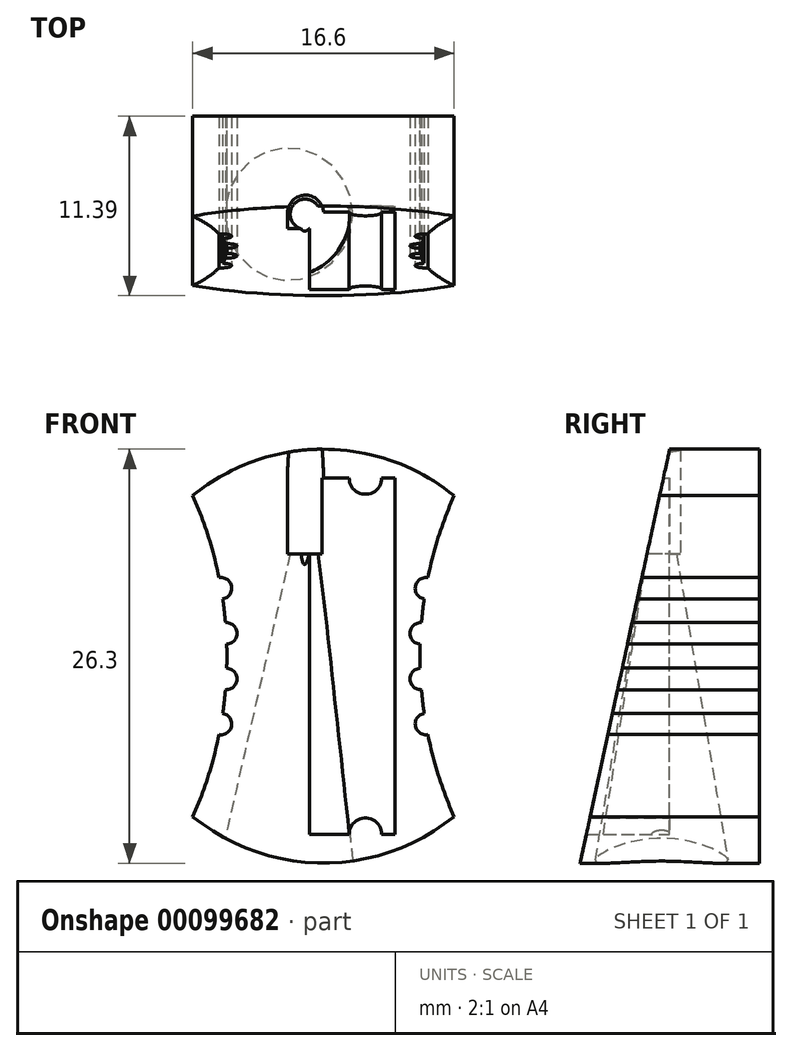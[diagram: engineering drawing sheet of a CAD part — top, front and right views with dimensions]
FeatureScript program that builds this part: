
annotation { "Feature Type Name" : "Feature", "Feature Type Description" : "" }
export const myFeature = defineFeature(function(context is Context, id is Id, definition is map)
    precondition{}
    {
        {
            var Q0;
            Q0=qCreatedBy(makeId("Front.planeOp"),FACE);
            var sketch = newSketch(context, id + "F0", { "sketchPlane" : qUnion([Q0])});
            skArc(sketch, "E0", {"start": v(-6.13, 0) * mm, "mid": v(-6.68, 5.21) * mm, "end": v(-8.3, 10.2) * mm});
            skPoint(sketch, "E0.first.point", {"position": v(-8.3, 10.2) * mm});
            skPoint(sketch, "E0.second.point", {"position": v(-6.13, 0) * mm});
            skPoint(sketch, "E0.third.point", {"position": v(-8.3, -10.2) * mm});
            skArc(sketch, "E1", {"start": v(0, 13.15) * mm, "mid": v(-4.4, 12.4) * mm, "end": v(-8.3, 10.2) * mm});
            skPoint(sketch, "E1.second.point", {"position": v(0, 13.15) * mm});
            skArc(sketch, "E2.MirrorCS", {"start": v(0, 13.15) * mm, "mid": v(4.4, 12.4) * mm, "end": v(8.3, 10.2) * mm});
            skArc(sketch, "E3.MirrorCS", {"start": v(6.13, 0) * mm, "mid": v(6.68, 5.21) * mm, "end": v(8.3, 10.2) * mm});
            skArc(sketch, "E4.MirrorCS", {"start": v(6.13, 0) * mm, "mid": v(6.68, -5.21) * mm, "end": v(8.3, -10.2) * mm});
            skArc(sketch, "E5.MirrorCS", {"start": v(0, -13.15) * mm, "mid": v(4.4, -12.4) * mm, "end": v(8.3, -10.2) * mm});
            skArc(sketch, "E6.MirrorCS", {"start": v(0, -13.15) * mm, "mid": v(-4.4, -12.4) * mm, "end": v(-8.3, -10.2) * mm});
            skArc(sketch, "E7.MirrorCS", {"start": v(-6.13, 0) * mm, "mid": v(-6.68, -5.21) * mm, "end": v(-8.3, -10.2) * mm});
            skSolve(sketch);
        }
        {
            var Q0;
            Q0 = qSketchRegion(id + "F0", true);
            extrude(context, id + "F1", {"entities" : qUnion([Q0]), "endBound" : BoundingType.SYMMETRIC, "depth" : 11.4 * mm});
        }
        {
            var Q0;
            Q0=qCreatedBy(makeId("Right.planeOp"),FACE);
            var sketch = newSketch(context, id + "F2", { "sketchPlane" : qUnion([Q0])});
            skLineSegment(sketch, "E8", {"start": v(0, 13.15) * mm, "end": v(-6, -14.56) * mm});
            skLineSegment(sketch, "E9", {"start": v(-6, -14.56) * mm, "end": v(-6, 13.15) * mm});
            skLineSegment(sketch, "E10", {"start": v(-6, 13.15) * mm, "end": v(0, 13.15) * mm});
            skSolve(sketch);
        }
        {
            var Q0;
            Q0=makeQuery(id+"F2.imprint","IMPRINT",FACE,{"disambiguationData":[TD([[makeQuery(id+"F2.imprint","IMPRINT",EDGE,{"derivedFrom":sQuery(id+"F2.wireOp",EDGE,"E8")}),-1.0]])]});
            var Q1;
            Q1=sQuery(id+"F2.wireOp",EDGE,"E10");
            extrude(context, id + "F3", {"entities" : qUnion([Q0]), "operationType" : NewBodyOperationType.REMOVE, "surfaceEntities" : qUnion([Q1]), "endBound" : BoundingType.SYMMETRIC, "oppositeDirection" : true, "depth" : 36.88 * mm});
        }
        {
            var Q0;
            Q0=qCreatedBy(makeId("Front.planeOp"),FACE);
            var sketch = newSketch(context, id + "F4", { "sketchPlane" : qUnion([Q0])});
            skCircle(sketch, "E11", {"center": v(-6.5, 4.3) * mm, "radius": 0.69 * mm});
            skCircle(sketch, "E12.MirrorC", {"center": v(-6.5, -4.3) * mm, "radius": 0.69 * mm});
            skCircle(sketch, "E13", {"center": v(-6.18, 1.45) * mm, "radius": 0.69 * mm});
            skCircle(sketch, "E14.MirrorC", {"center": v(-6.18, -1.45) * mm, "radius": 0.69 * mm});
            skCircle(sketch, "E15.MirrorC", {"center": v(6.5, 4.3) * mm, "radius": 0.69 * mm});
            skCircle(sketch, "E16.MirrorC", {"center": v(6.18, 1.45) * mm, "radius": 0.69 * mm});
            skCircle(sketch, "E17.MirrorC", {"center": v(6.18, -1.45) * mm, "radius": 0.69 * mm});
            skCircle(sketch, "E18.MirrorC", {"center": v(6.5, -4.3) * mm, "radius": 0.69 * mm});
            skSolve(sketch);
        }
        {
            var Q0;
            Q0 = qSketchRegion(id + "F4", true);
            extrude(context, id + "F5", {"entities" : qUnion([Q0]), "operationType" : NewBodyOperationType.REMOVE, "endBound" : BoundingType.SYMMETRIC, "oppositeDirection" : true, "depth" : 30.96 * mm});
        }
        {
            var Q0;
            Q0=qCreatedBy(makeId("Front.planeOp"),FACE);
            var sketch = newSketch(context, id + "F6", { "sketchPlane" : qUnion([Q0])});
            skLineSegment(sketch, "E19", {"start": v(4.56, 11.32) * mm, "end": v(4.56, 0) * mm});
            skLineSegment(sketch, "E20", {"start": v(-0.9, 0) * mm, "end": v(-0.9, 11.32) * mm});
            skLineSegment(sketch, "E21", {"start": v(-0.9, 11.32) * mm, "end": v(1.63, 11.32) * mm});
            skLineSegment(sketch, "E22.MirrorCS", {"start": v(4.56, -11.32) * mm, "end": v(4.56, 0) * mm});
            skLineSegment(sketch, "E23.MirrorCS", {"start": v(-0.9, -11.32) * mm, "end": v(1.63, -11.32) * mm});
            skLineSegment(sketch, "E24.MirrorCS", {"start": v(-0.9, 0) * mm, "end": v(-0.9, -11.32) * mm});
            skArc(sketch, "E25", {"start": v(1.63, 11.32) * mm, "mid": v(2.66, 10.28) * mm, "end": v(3.7, 11.32) * mm});
            skArc(sketch, "E26.MirrorC", {"start": v(1.63, -11.32) * mm, "mid": v(2.66, -10.28) * mm, "end": v(3.7, -11.32) * mm});
            skLineSegment(sketch, "E27.trimOffspring", {"start": v(3.7, -11.32) * mm, "end": v(4.56, -11.32) * mm});
            skLineSegment(sketch, "E28.trimOffspring", {"start": v(3.7, 11.32) * mm, "end": v(4.56, 11.32) * mm});
            skSolve(sketch);
        }
        {
            var Q0;
            Q0 = qSketchRegion(id + "F6", true);
            extrude(context, id + "F7", {"entities" : qUnion([Q0]), "operationType" : NewBodyOperationType.REMOVE, "depth" : 25 * mm});
        }
        {
            var Q0;
            Q0=qCreatedBy(makeId("Top.planeOp"),FACE);
            cPlane(context, id + "F8", {"entities" : qUnion([Q0]), "cplaneType" : CPlaneType.OFFSET, "offset" : 6.5 * mm, "width" : 150 * mm, "height" : 150 * mm});
        }
        {
            var Q0;
            Q0=qCreatedBy(id+"F8.planeOp",FACE);
            cPlane(context, id + "F9", {"entities" : qUnion([Q0]), "cplaneType" : CPlaneType.OFFSET, "offset" : 20 * mm, "oppositeDirection" : true, "width" : 150 * mm, "height" : 150 * mm});
        }
        {
            var Q0;
            Q0=qCreatedBy(id+"F9.planeOp",FACE);
            var sketch = newSketch(context, id + "F10", { "sketchPlane" : qUnion([Q0])});
            skCircle(sketch, "E29", {"center": v(-2.39, -0.52) * mm, "radius": 4.3 * mm});
            skSolve(sketch);
        }
        {
            var Q0;
            Q0=qCreatedBy(id+"F8.planeOp",FACE);
            var sketch = newSketch(context, id + "F11", { "sketchPlane" : qUnion([Q0])});
            skCircle(sketch, "E30", {"center": v(-1.16, -0.52) * mm, "radius": 0.96 * mm});
            skSolve(sketch);
        }
        {
            var Q1;
            Q1 = qSketchRegion(id + "F10", true);
            var Q2;
            Q2 = qSketchRegion(id + "F11", true);
            loft(context, id + "F12", {"operationType" : NewBodyOperationType.REMOVE, "sheetProfilesArray" : [{ "sheetProfileEntities" : qUnion([Q1]) }, { "sheetProfileEntities" : qUnion([Q2]) }]});
        }
        {
            var Q0;
            Q0=qCreatedBy(id+"F8.planeOp",FACE);
            var sketch = newSketch(context, id + "F13", { "sketchPlane" : qUnion([Q0])});
            skArc(sketch, "E31", {"start": v(0, -0.36) * mm, "mid": v(-1.19, 0.7) * mm, "end": v(-2.29, -0.45) * mm});
            skLineSegment(sketch, "E32", {"start": v(-2.29, -0.45) * mm, "end": v(-2.29, -5.76) * mm});
            skLineSegment(sketch, "E33", {"start": v(-2.29, -5.76) * mm, "end": v(0, -5.76) * mm});
            skLineSegment(sketch, "E34", {"start": v(0, -5.76) * mm, "end": v(0, -0.36) * mm});
            skSolve(sketch);
        }
        {
            var Q0;
            Q0 = qSketchRegion(id + "F13", true);
            extrude(context, id + "F14", {"entities" : qUnion([Q0]), "operationType" : NewBodyOperationType.REMOVE, "depth" : 25 * mm});
        }
    });
